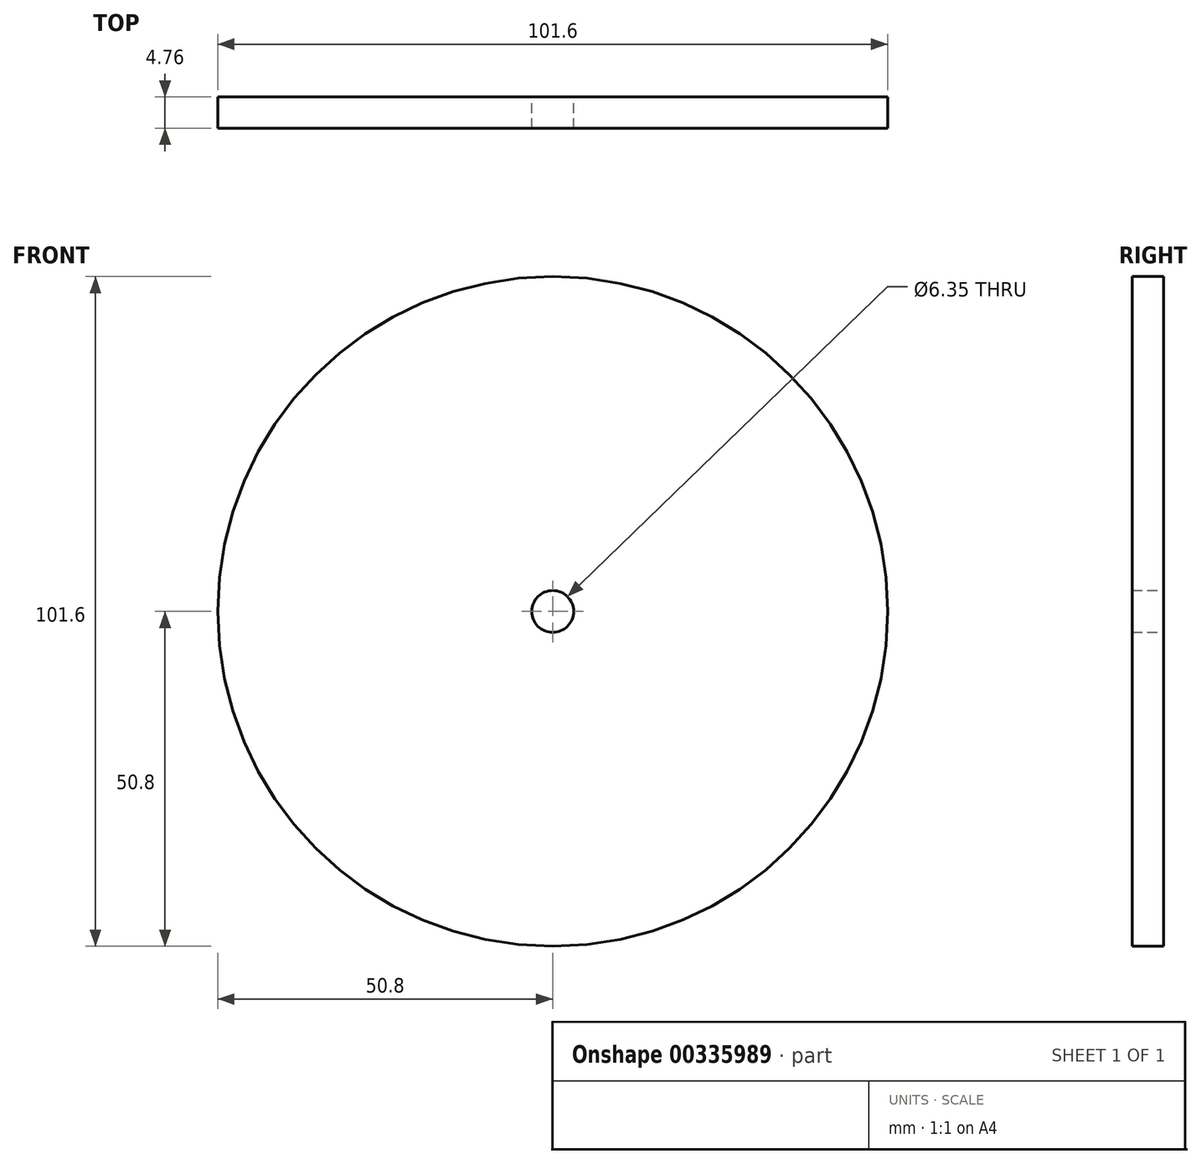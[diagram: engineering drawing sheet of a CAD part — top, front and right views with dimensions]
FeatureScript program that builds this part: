
annotation { "Feature Type Name" : "Feature", "Feature Type Description" : "" }
export const myFeature = defineFeature(function(context is Context, id is Id, definition is map)
    precondition{}
    {
        {
            var Q0;
            Q0=qCreatedBy(makeId("Front.planeOp"),FACE);
            var sketch = newSketch(context, id + "F0", { "sketchPlane" : qUnion([Q0])});
            skCircle(sketch, "E0", {"center": v(0, 0) * mm, "radius": 50.8 * mm});
            skCircle(sketch, "E1", {"center": v(0, 0) * mm, "radius": 3.17 * mm});
            skSolve(sketch);
        }
        {
            var Q0;
            Q0=makeQuery(id+"F0.imprint","IMPRINT",FACE,{"disambiguationData":[TD([[makeQuery(id+"F0.imprint","IMPRINT",EDGE,{"derivedFrom":sQuery(id+"F0.wireOp",EDGE,"E0")}),1.0]])]});
            extrude(context, id + "F1", {"entities" : qUnion([Q0]), "endBound" : BoundingType.SYMMETRIC, "depth" : 4.76 * mm});
        }
    });
